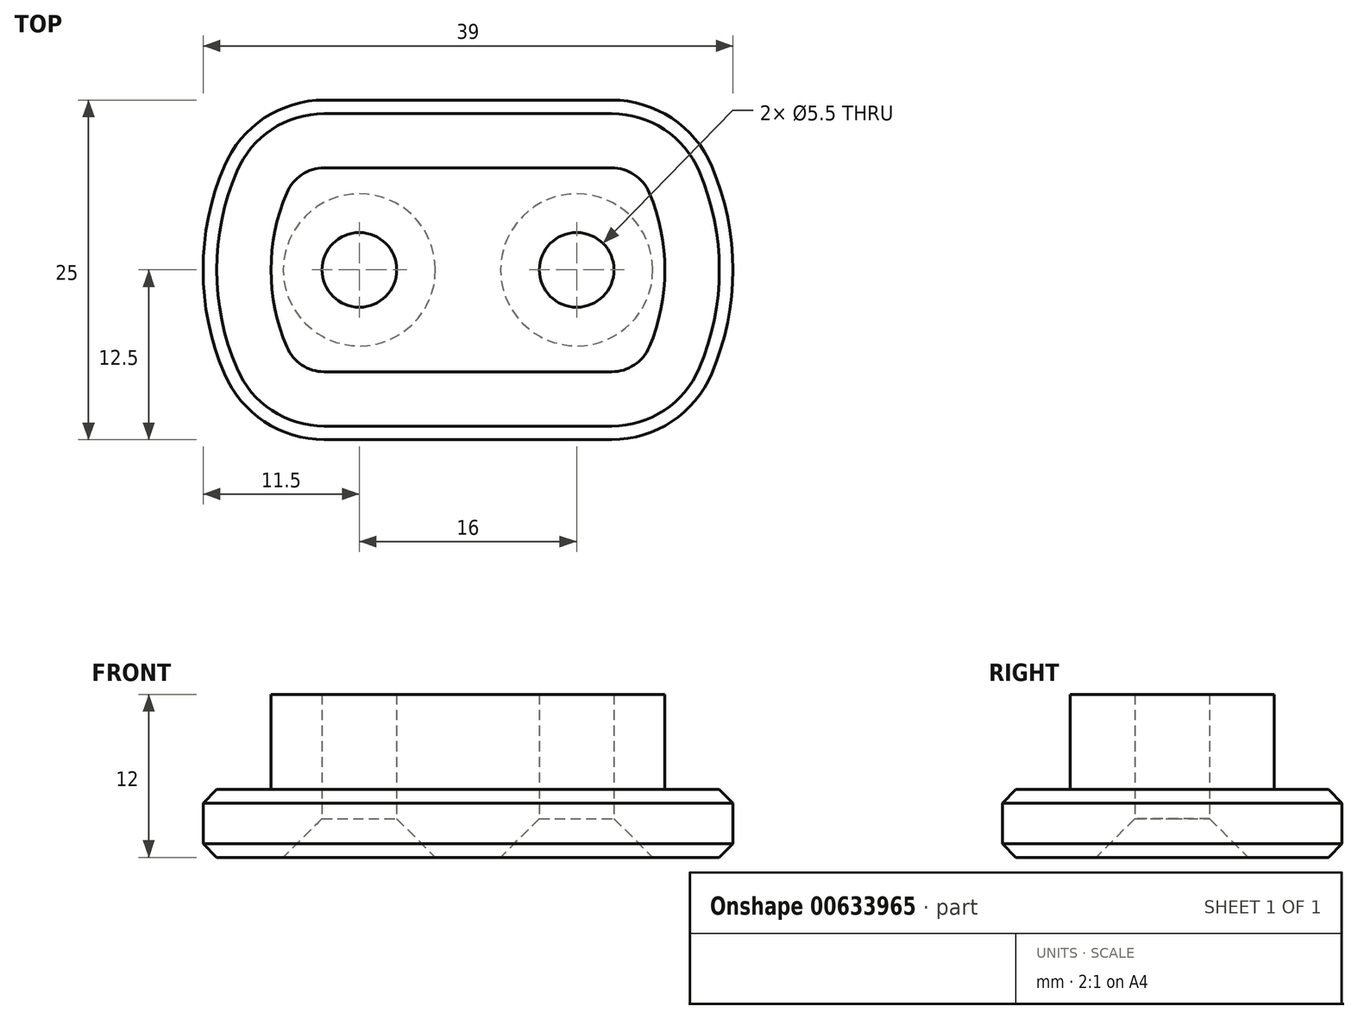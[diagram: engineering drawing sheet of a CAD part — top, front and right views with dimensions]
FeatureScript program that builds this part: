
annotation { "Feature Type Name" : "Feature", "Feature Type Description" : "" }
export const myFeature = defineFeature(function(context is Context, id is Id, definition is map)
    precondition{}
    {
        {
            var Q0;
            Q0=qCreatedBy(makeId("Top.planeOp"),FACE);
            var sketch = newSketch(context, id + "F0", { "sketchPlane" : qUnion([Q0])});
            skArc(sketch, "E0", {"start": v(-12.4, 7.5) * mm, "mid": v(-14.5, 0) * mm, "end": v(-12.4, -7.5) * mm});
            skLineSegment(sketch, "E1.bottom", {"start": v(25, 7.5) * mm, "end": v(-25, 7.5) * mm, "construction": true});
            skLineSegment(sketch, "E1.top", {"start": v(25, -7.5) * mm, "end": v(-25, -7.5) * mm, "construction": true});
            skLineSegment(sketch, "E1.left", {"start": v(25, 7.5) * mm, "end": v(25, -7.5) * mm, "construction": true});
            skLineSegment(sketch, "E1.right", {"start": v(-25, 7.5) * mm, "end": v(-25, -7.5) * mm, "construction": true});
            skArc(sketch, "E2.trimOffspring", {"start": v(12.4, -7.5) * mm, "mid": v(14.5, 0) * mm, "end": v(12.4, 7.5) * mm});
            skLineSegment(sketch, "E3", {"start": v(-12.4, 7.5) * mm, "end": v(12.4, 7.5) * mm});
            skLineSegment(sketch, "E4", {"start": v(-12.4, -7.5) * mm, "end": v(12.4, -7.5) * mm});
            skSolve(sketch);
        }
        {
            var Q0;
            Q0=makeQuery(id+"F0.imprint","IMPRINT",FACE,{"disambiguationData":[TD([[makeQuery(id+"F0.imprint","IMPRINT",EDGE,{"derivedFrom":sQuery(id+"F0.wireOp",EDGE,"E0")}),1.0]])]});
            extrude(context, id + "F1", {"entities" : qUnion([Q0]), "depth" : 7 * mm, "offsetDistance" : 25 * mm});
        }
        {
            var Q0;
            Q0=makeQuery(id+"F1.opExtrude","CAP_FACE",FACE,{"disambiguationData":[OSD([sQuery(id+"F0.wireOp",EDGE,"E0"),sQuery(id+"F0.wireOp",EDGE,"E2.trimOffspring"),sQuery(id+"F0.wireOp",EDGE,"E3"),sQuery(id+"F0.wireOp",EDGE,"E4")])],"isStart":true});
            var sketch = newSketch(context, id + "F2", { "sketchPlane" : qUnion([Q0])});
            skLineSegment(sketch, "E5.0", {"start": v(-14.97, 12.5) * mm, "end": v(14.97, 12.5) * mm});
            skArc(sketch, "E5.1", {"start": v(-14.97, -12.5) * mm, "mid": v(-19.5, 0) * mm, "end": v(-14.97, 12.5) * mm});
            skLineSegment(sketch, "E5.2", {"start": v(-14.97, -12.5) * mm, "end": v(14.97, -12.5) * mm});
            skArc(sketch, "E5.3", {"start": v(14.97, 12.5) * mm, "mid": v(19.5, 0) * mm, "end": v(14.97, -12.5) * mm});
            skSolve(sketch);
        }
        {
            var Q0;
            Q0=makeQuery(id+"F2.imprint","IMPRINT",FACE,{"disambiguationData":[TD([[makeQuery(id+"F2.imprint","IMPRINT",EDGE,{"derivedFrom":sQuery(id+"F2.wireOp",EDGE,"E5.0")}),-1.0]])]});
            var Q1;
            Q1=makeQuery(id+"F2.imprint","IMPRINT",FACE,{"disambiguationData":[TD([[makeQuery(id+"F2.imprint","IMPRINT",EDGE,{"derivedFrom":makeQuery(id+"F1.opExtrude","CAP_EDGE",EDGE,{"disambiguationData":[OSD([sQuery(id+"F0.wireOp",EDGE,"E0")])],"isStart":true})}),-1.0]])]});
            extrude(context, id + "F3", {"entities" : qUnion([Q0, Q1]), "operationType" : NewBodyOperationType.ADD, "depth" : 5 * mm, "offsetDistance" : 25 * mm});
        }
        {
            var Q0;
            Q0=makeQuery(id+"F3.opExtrude","CAP_FACE",FACE,{"disambiguationData":[OSD([sQuery(id+"F2.wireOp",EDGE,"E5.0"),sQuery(id+"F2.wireOp",EDGE,"E5.1"),sQuery(id+"F2.wireOp",EDGE,"E5.2"),sQuery(id+"F2.wireOp",EDGE,"E5.3")])],"isStart":false});
            var sketch = newSketch(context, id + "F4", { "sketchPlane" : qUnion([Q0])});
            skLineSegment(sketch, "E6", {"start": v(0, 12.5) * mm, "end": v(0, -12.5) * mm, "construction": true});
            skLineSegment(sketch, "E7", {"start": v(-8, 0) * mm, "end": v(8, 0) * mm, "construction": true});
            skPoint(sketch, "E8", {"position": v(0, 0) * mm});
            skSolve(sketch);
        }
        {
            var Q0;
            Q0=sQuery(id+"F4.wireOp",VERTEX,"E7.start");
            var Q1;
            Q1=sQuery(id+"F4.wireOp",VERTEX,"E7.end");
            var Q2;
            Q2=makeQuery(id+"F1.opExtrude","SWEPT_BODY",BODY,{"disambiguationData":[OSD([sQuery(id+"F0.wireOp",EDGE,"E0")])]});
            hole(context, id + "F5", {"style" : HoleStyle.C_SINK, "endStyle" : HoleEndStyle.THROUGH, "standardTappedOrClearance" : lookupTablePath({ "standard" : "ISO", "fit" : "Normal", "size" : "M5", "type" : "Clearance" }), "standardBlindInLast" : lookupTablePath({ "fit" : "Standard", "standard" : "ISO", "size" : "M5", "type" : "Clearance" }), "holeDiameter" : 5.5 * mm, "cSinkDiameter" : 11.2 * mm, "cSinkAngle" : 90 * degree, "majorDiameter" : 5 * mm, "isTappedThrough" : true, "tappedDepth" : 12 * mm, "tapClearance" : 3, "locations" : qUnion([Q0, Q1]), "scope" : qUnion([Q2])});
        }
        {
            var Q0;
            Q0=makeQuery(id+"F3.opExtrude","SWEPT_EDGE",EDGE,{"disambiguationData":[OSD([sQuery(id+"F2.wireOp",EDGE,"E5.0"),sQuery(id+"F2.wireOp",EDGE,"E5.3")])]});
            var Q1;
            Q1=makeQuery(id+"F3.opExtrude","SWEPT_EDGE",EDGE,{"disambiguationData":[OSD([sQuery(id+"F2.wireOp",EDGE,"E5.2"),sQuery(id+"F2.wireOp",EDGE,"E5.3")])]});
            var Q2;
            Q2=makeQuery(id+"F3.opExtrude","SWEPT_EDGE",EDGE,{"disambiguationData":[OSD([sQuery(id+"F2.wireOp",EDGE,"E5.1"),sQuery(id+"F2.wireOp",EDGE,"E5.2")])]});
            var Q3;
            Q3=makeQuery(id+"F3.opExtrude","SWEPT_EDGE",EDGE,{"disambiguationData":[OSD([sQuery(id+"F2.wireOp",EDGE,"E5.0"),sQuery(id+"F2.wireOp",EDGE,"E5.1")])]});
            fillet(context, id + "F6", {"entities" : qUnion([Q0, Q1, Q2, Q3]), "radius" : 8 * mm, "tangentPropagation" : true, "allowEdgeOverflow" : false});
        }
        {
            var Q0;
            Q0=makeQuery(id+"F1.opExtrude","SWEPT_EDGE",EDGE,{"disambiguationData":[OSD([sQuery(id+"F0.wireOp",EDGE,"E2.trimOffspring"),sQuery(id+"F0.wireOp",EDGE,"E4")])]});
            var Q1;
            Q1=makeQuery(id+"F1.opExtrude","SWEPT_EDGE",EDGE,{"disambiguationData":[OSD([sQuery(id+"F0.wireOp",EDGE,"E2.trimOffspring"),sQuery(id+"F0.wireOp",EDGE,"E3")])]});
            var Q2;
            Q2=makeQuery(id+"F1.opExtrude","SWEPT_EDGE",EDGE,{"disambiguationData":[OSD([sQuery(id+"F0.wireOp",EDGE,"E0"),sQuery(id+"F0.wireOp",EDGE,"E3")])]});
            var Q3;
            Q3=makeQuery(id+"F1.opExtrude","SWEPT_EDGE",EDGE,{"disambiguationData":[OSD([sQuery(id+"F0.wireOp",EDGE,"E0"),sQuery(id+"F0.wireOp",EDGE,"E4")])]});
            fillet(context, id + "F7", {"entities" : qUnion([Q0, Q1, Q2, Q3]), "radius" : 3 * mm, "tangentPropagation" : true, "allowEdgeOverflow" : false});
        }
        {
            var Q0;
            Q0=makeQuery(id+"F3.opExtrude","CAP_EDGE",EDGE,{"disambiguationData":[OSD([sQuery(id+"F2.wireOp",EDGE,"E5.0")])],"isStart":false});
            var Q1;
            Q1=makeQuery(id+"F3.opExtrude","CAP_EDGE",EDGE,{"disambiguationData":[OSD([sQuery(id+"F2.wireOp",EDGE,"E5.1")])],"isStart":false});
            var Q2;
            Q2=makeQuery(id+"F3.opExtrude","CAP_EDGE",EDGE,{"disambiguationData":[OSD([sQuery(id+"F2.wireOp",EDGE,"E5.2")])],"isStart":false});
            var Q3;
            Q3=makeQuery(id+"F3.opExtrude","CAP_EDGE",EDGE,{"disambiguationData":[OSD([sQuery(id+"F2.wireOp",EDGE,"E5.3")])],"isStart":false});
            var Q4;
            Q4=makeQuery(id+"F3.opExtrude","CAP_EDGE",EDGE,{"disambiguationData":[OSD([sQuery(id+"F2.wireOp",EDGE,"E5.3")])],"isStart":true});
            var Q5;
            Q5=makeQuery(id+"F3.opExtrude","CAP_EDGE",EDGE,{"disambiguationData":[OSD([sQuery(id+"F2.wireOp",EDGE,"E5.0")])],"isStart":true});
            var Q6;
            Q6=makeQuery(id+"F3.opExtrude","CAP_EDGE",EDGE,{"disambiguationData":[OSD([sQuery(id+"F2.wireOp",EDGE,"E5.1")])],"isStart":true});
            var Q7;
            Q7=makeQuery(id+"F3.opExtrude","CAP_EDGE",EDGE,{"disambiguationData":[OSD([sQuery(id+"F2.wireOp",EDGE,"E5.2")])],"isStart":true});
            chamfer(context, id + "F8", {"entities" : qUnion([Q0, Q1, Q2, Q3, Q4, Q5, Q6, Q7]), "width" : 1 * mm, "tangentPropagation" : true});
        }
    });
